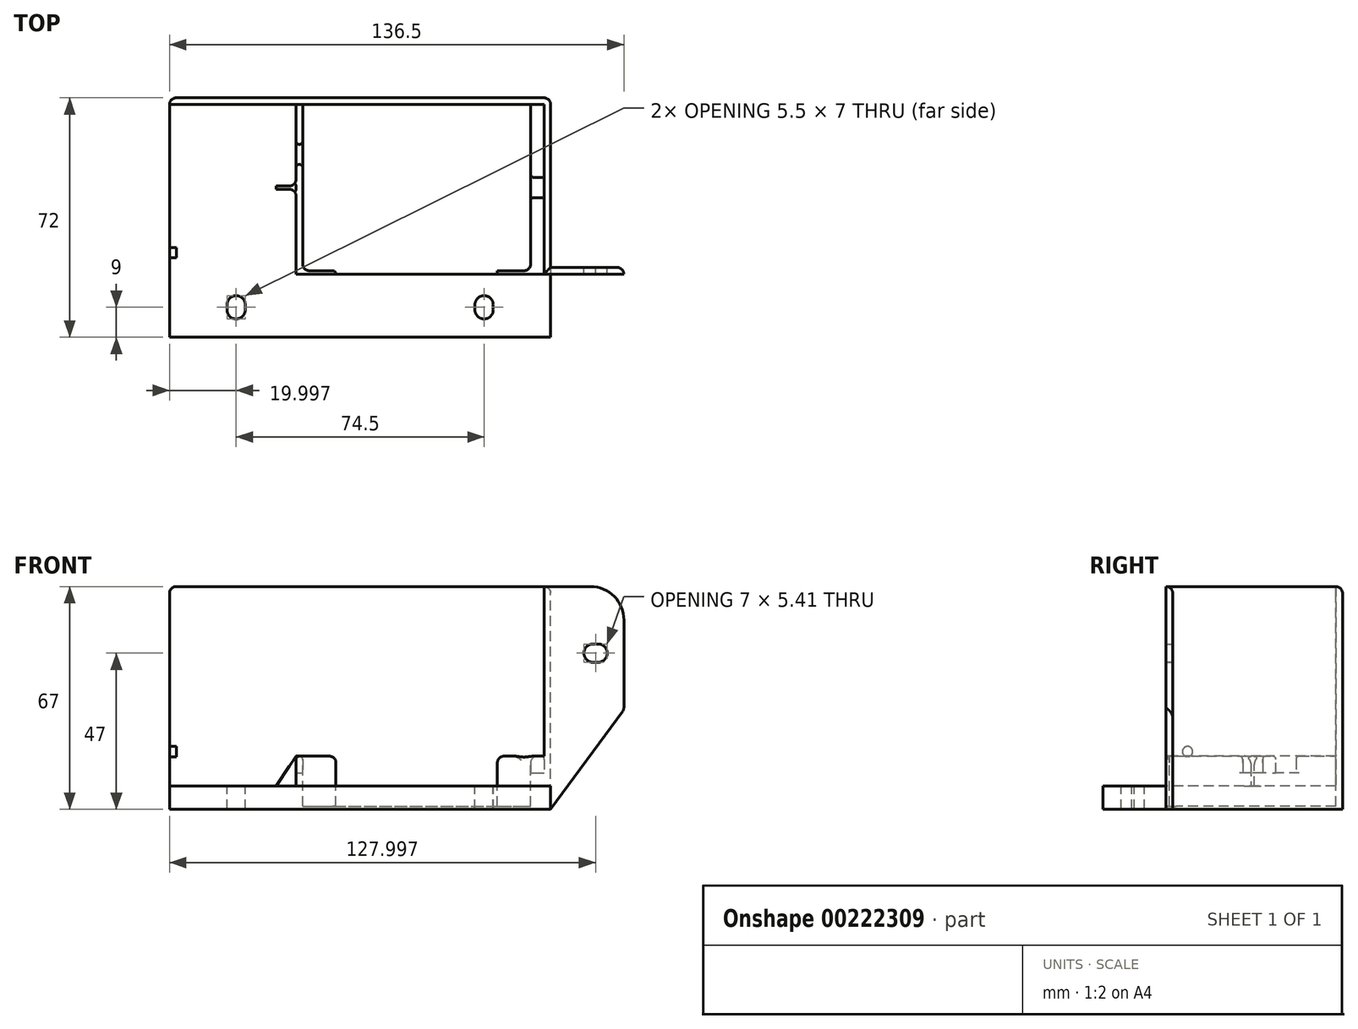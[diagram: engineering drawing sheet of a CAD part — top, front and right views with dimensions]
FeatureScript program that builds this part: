
annotation { "Feature Type Name" : "Feature", "Feature Type Description" : "" }
export const myFeature = defineFeature(function(context is Context, id is Id, definition is map)
    precondition{}
    {
        {
            var Q0;
            Q0=qCreatedBy(makeId("Top.planeOp"),FACE);
            var sketch = newSketch(context, id + "F0", { "sketchPlane" : qUnion([Q0])});
            skLineSegment(sketch, "E0.bottom", {"start": v(-55.25, 40.13) * mm, "end": v(59.25, 40.13) * mm});
            skLineSegment(sketch, "E0.top", {"start": v(-55.25, -31.87) * mm, "end": v(59.25, -31.87) * mm});
            skLineSegment(sketch, "E0.left", {"start": v(-55.25, 40.13) * mm, "end": v(-55.25, -31.87) * mm});
            skLineSegment(sketch, "E0.right", {"start": v(59.25, 40.13) * mm, "end": v(59.25, -31.87) * mm});
            skLineSegment(sketch, "E1", {"start": v(-55.25, -12.87) * mm, "end": v(59.25, -12.87) * mm, "construction": true});
            skLineSegment(sketch, "E2", {"start": v(-53.25, -12.87) * mm, "end": v(-53.25, 38.13) * mm});
            skLineSegment(sketch, "E3", {"start": v(-53.25, 38.13) * mm, "end": v(57.25, 38.13) * mm});
            skLineSegment(sketch, "E4", {"start": v(57.25, 38.13) * mm, "end": v(57.25, -12.87) * mm});
            skLineSegment(sketch, "E5", {"start": v(-55.25, -12.87) * mm, "end": v(-53.25, -12.87) * mm});
            skLineSegment(sketch, "E6", {"start": v(59.25, -12.87) * mm, "end": v(57.25, -12.87) * mm});
            skLineSegment(sketch, "E7", {"start": v(-55.25, -22.87) * mm, "end": v(59.25, -22.87) * mm, "construction": true});
            skCircle(sketch, "E8", {"center": v(-35.25, -22.87) * mm, "radius": 2.75 * mm});
            skCircle(sketch, "E9", {"center": v(39.25, -22.87) * mm, "radius": 2.75 * mm});
            skLineSegment(sketch, "E10", {"start": v(-15.25, 38.13) * mm, "end": v(-15.25, -11.87) * mm});
            skLineSegment(sketch, "E11", {"start": v(-15.25, -11.87) * mm, "end": v(-5.25, -11.87) * mm});
            skLineSegment(sketch, "E12", {"start": v(-17.25, 38.13) * mm, "end": v(-17.25, -12.87) * mm});
            skLineSegment(sketch, "E13", {"start": v(-17.25, -12.87) * mm, "end": v(57.25, -12.87) * mm});
            skLineSegment(sketch, "E14", {"start": v(53.25, 38.13) * mm, "end": v(53.25, -11.87) * mm});
            skLineSegment(sketch, "E15", {"start": v(53.25, 13.13) * mm, "end": v(57.25, 13.13) * mm, "construction": true});
            skLineSegment(sketch, "E16", {"start": v(53.25, 16.13) * mm, "end": v(57.25, 16.13) * mm});
            skLineSegment(sketch, "E17.MirrorCS", {"start": v(53.25, 10.13) * mm, "end": v(57.25, 10.13) * mm});
            skLineSegment(sketch, "E18", {"start": v(-17.25, 26.13) * mm, "end": v(-15.25, 26.13) * mm});
            skLineSegment(sketch, "E19", {"start": v(-17.25, 20.13) * mm, "end": v(-15.25, 20.13) * mm});
            skLineSegment(sketch, "E20", {"start": v(59.25, -12.87) * mm, "end": v(81.25, -12.87) * mm});
            skLineSegment(sketch, "E21", {"start": v(81.25, -12.87) * mm, "end": v(81.25, -10.87) * mm});
            skLineSegment(sketch, "E22", {"start": v(81.25, -10.87) * mm, "end": v(59.25, -10.87) * mm});
            skCircle(sketch, "E23", {"center": v(-35.25, -22.12) * mm, "radius": 2.75 * mm});
            skCircle(sketch, "E24", {"center": v(39.25, -22.12) * mm, "radius": 2.75 * mm});
            skCircle(sketch, "E25.MirrorC", {"center": v(-35.25, -23.62) * mm, "radius": 2.75 * mm});
            skCircle(sketch, "E26.MirrorC", {"center": v(39.25, -23.62) * mm, "radius": 2.75 * mm});
            skLineSegment(sketch, "E27", {"start": v(-5.25, -11.87) * mm, "end": v(-5.25, -12.87) * mm});
            skLineSegment(sketch, "E28", {"start": v(43.25, -11.87) * mm, "end": v(43.25, -12.87) * mm});
            skLineSegment(sketch, "E29.trimOffspring", {"start": v(43.25, -11.87) * mm, "end": v(57.25, -11.87) * mm});
            skPoint(sketch, "E30.oppositeSnap0", {"position": v(-17.25, 12.63) * mm});
            skLineSegment(sketch, "E30.bottom", {"start": v(-17.25, 13.63) * mm, "end": v(-27.25, 13.63) * mm});
            skLineSegment(sketch, "E30.top", {"start": v(-17.25, 12.63) * mm, "end": v(-27.25, 12.63) * mm});
            skLineSegment(sketch, "E30.left", {"start": v(-17.25, 13.63) * mm, "end": v(-17.25, 12.63) * mm});
            skLineSegment(sketch, "E30.right", {"start": v(-27.25, 13.63) * mm, "end": v(-27.25, 12.63) * mm});
            skSolve(sketch);
        }
        {
            var Q0;
            {var subQ9=sQuery(id+"F0.wireOp",EDGE,"E0.bottom");Q0=makeQuery(id+"F0.imprint","IMPRINT",FACE,{"disambiguationData":[TD([[makeQuery(id+"F0.imprint","IMPRINT",EDGE,{"derivedFrom":subQ9}),-1.0]])]});}
            var Q1;
            {var subQ28=sQuery(id+"F0.wireOp",EDGE,"E0.top");Q1=makeQuery(id+"F0.imprint","IMPRINT",FACE,{"disambiguationData":[TD([[makeQuery(id+"F0.imprint","IMPRINT",EDGE,{"derivedFrom":subQ28}),1.0]])]});}
            var Q2;
            {var subQ5=sQuery(id+"F0.wireOp",EDGE,"E18");Q2=makeQuery(id+"F0.imprint","IMPRINT",FACE,{"disambiguationData":[TD([[makeQuery(id+"F0.imprint","IMPRINT",EDGE,{"derivedFrom":subQ5}),1.0]])]});}
            var Q3;
            {var subQ0=sQuery(id+"F0.wireOp",EDGE,"E18");Q3=makeQuery(id+"F0.imprint","IMPRINT",FACE,{"disambiguationData":[TD([[makeQuery(id+"F0.imprint","IMPRINT",EDGE,{"derivedFrom":subQ0}),-1.0]])]});}
            var Q4;
            {var subQ2=sQuery(id+"F0.wireOp",EDGE,"E28");Q4=makeQuery(id+"F0.imprint","IMPRINT",FACE,{"disambiguationData":[TD([[makeQuery(id+"F0.imprint","IMPRINT",EDGE,{"derivedFrom":subQ2}),1.0]])]});}
            var Q5;
            {var subQ10=sQuery(id+"F0.wireOp",EDGE,"E11");Q5=makeQuery(id+"F0.imprint","IMPRINT",FACE,{"disambiguationData":[TD([[makeQuery(id+"F0.imprint","IMPRINT",EDGE,{"derivedFrom":subQ10}),1.0]])]});}
            var Q6;
            {var subQ5=sQuery(id+"F0.wireOp",EDGE,"E16");Q6=makeQuery(id+"F0.imprint","IMPRINT",FACE,{"disambiguationData":[TD([[makeQuery(id+"F0.imprint","IMPRINT",EDGE,{"derivedFrom":subQ5}),1.0]])]});}
            var Q7;
            {var subQ0=sQuery(id+"F0.wireOp",EDGE,"E16");Q7=makeQuery(id+"F0.imprint","IMPRINT",FACE,{"disambiguationData":[TD([[makeQuery(id+"F0.imprint","IMPRINT",EDGE,{"derivedFrom":subQ0}),-1.0]])]});}
            var Q8;
            {var subQ0=sQuery(id+"F0.wireOp",EDGE,"E17.MirrorCS");Q8=makeQuery(id+"F0.imprint","IMPRINT",FACE,{"disambiguationData":[TD([[makeQuery(id+"F0.imprint","IMPRINT",EDGE,{"derivedFrom":subQ0}),-1.0]])]});}
            var Q9;
            {var subQ4=sQuery(id+"F0.wireOp",EDGE,"E11");Q9=makeQuery(id+"F0.imprint","IMPRINT",FACE,{"disambiguationData":[TD([[makeQuery(id+"F0.imprint","IMPRINT",EDGE,{"derivedFrom":subQ4}),-1.0]])]});}
            var Q10;
            Q10=makeQuery(id+"F0.imprint","IMPRINT",FACE,{"disambiguationData":[TD([[makeQuery(id+"F0.imprint","IMPRINT",EDGE,{"derivedFrom":sQuery(id+"F0.wireOp",EDGE,"E30.bottom")}),1.0]])]});
            var Q11;
            {var subQ0=sQuery(id+"F0.wireOp",EDGE,"E20");Q11=makeQuery(id+"F0.imprint","IMPRINT",FACE,{"disambiguationData":[TD([[makeQuery(id+"F0.imprint","IMPRINT",EDGE,{"derivedFrom":subQ0}),1.0]])]});}
            extrude(context, id + "F1", {"entities" : qUnion([Q0, Q1, Q2, Q3, Q4, Q5, Q6, Q7, Q8, Q9, Q10, Q11]), "oppositeDirection" : true, "depth" : 7 * mm});
        }
        {
            var Q0;
            {var subQ1=sQuery(id+"F0.wireOp",EDGE,"E0.bottom");Q0=makeQuery(id+"F0.imprint","IMPRINT",FACE,{"disambiguationData":[TD([[makeQuery(id+"F0.imprint","IMPRINT",EDGE,{"derivedFrom":subQ1}),-1.0]])]});}
            extrude(context, id + "F2", {"entities" : qUnion([Q0]), "operationType" : NewBodyOperationType.ADD, "depth" : 60 * mm});
        }
        {
            var Q0;
            {var subQ10=sQuery(id+"F0.wireOp",EDGE,"E11");Q0=makeQuery(id+"F0.imprint","IMPRINT",FACE,{"disambiguationData":[TD([[makeQuery(id+"F0.imprint","IMPRINT",EDGE,{"derivedFrom":subQ10}),1.0]])]});}
            extrude(context, id + "F3", {"entities" : qUnion([Q0]), "operationType" : NewBodyOperationType.REMOVE, "oppositeDirection" : true, "depth" : 6 * mm});
        }
        {
            var Q0;
            Q0=makeQuery(id+"F2.opExtrude","CAP_FACE",FACE,{"disambiguationData":[OSD([sQuery(id+"F0.wireOp",EDGE,"E0.bottom"),sQuery(id+"F0.wireOp",EDGE,"E0.left"),sQuery(id+"F0.wireOp",EDGE,"E0.right"),sQuery(id+"F0.wireOp",EDGE,"E2"),sQuery(id+"F0.wireOp",EDGE,"E3"),sQuery(id+"F0.wireOp",EDGE,"E4"),sQuery(id+"F0.wireOp",EDGE,"E5"),sQuery(id+"F0.wireOp",EDGE,"E6")])],"isStart":false});
            var sketch = newSketch(context, id + "F4", { "sketchPlane" : qUnion([Q0])});
            skPoint(sketch, "E31.0", {"position": v(-55.25, 13.63) * mm});
            skLineSegment(sketch, "E32.0", {"start": v(-55.25, 40.13) * mm, "end": v(-55.25, -12.87) * mm, "construction": true});
            skLineSegment(sketch, "E33.0", {"start": v(-53.25, -12.87) * mm, "end": v(-53.25, 38.13) * mm, "construction": true});
            skLineSegment(sketch, "E34.0", {"start": v(-55.25, -12.87) * mm, "end": v(-53.25, -12.87) * mm, "construction": true});
            skLineSegment(sketch, "E35", {"start": v(-53.25, 12.63) * mm, "end": v(-55.25, 12.63) * mm, "construction": true});
            skLineSegment(sketch, "E36", {"start": v(-55.25, 6.63) * mm, "end": v(-53.25, 6.63) * mm});
            skLineSegment(sketch, "E37.MirrorCS", {"start": v(-55.25, 18.63) * mm, "end": v(-53.25, 18.63) * mm});
            skLineSegment(sketch, "E38", {"start": v(-55.25, 18.63) * mm, "end": v(-55.25, 6.63) * mm});
            skLineSegment(sketch, "E39", {"start": v(-53.25, 18.63) * mm, "end": v(-53.25, 6.63) * mm});
            skSolve(sketch);
        }
        {
            var Q0;
            Q0=makeQuery(id+"F4.imprint","IMPRINT",FACE,{"disambiguationData":[TD([[makeQuery(id+"F4.imprint","IMPRINT",EDGE,{"derivedFrom":sQuery(id+"F4.wireOp",EDGE,"E36")}),1.0]])]});
            extrude(context, id + "F5", {"entities" : qUnion([Q0]), "operationType" : NewBodyOperationType.ADD, "depth" : 6 * mm});
        }
        {
            var Q0;
            Q0=makeQuery(id+"F5.opExtrude","CAP_EDGE",EDGE,{"disambiguationData":[OSD([sQuery(id+"F4.wireOp",EDGE,"E36")])],"isStart":true});
            var Q1;
            Q1=makeQuery(id+"F5.opExtrude","CAP_EDGE",EDGE,{"disambiguationData":[OSD([sQuery(id+"F4.wireOp",EDGE,"E36")])],"isStart":false});
            var Q2;
            Q2=makeQuery(id+"F5.opExtrude","CAP_EDGE",EDGE,{"disambiguationData":[OSD([sQuery(id+"F4.wireOp",EDGE,"E37.MirrorCS")])],"isStart":false});
            var Q3;
            Q3=makeQuery(id+"F5.opExtrude","CAP_EDGE",EDGE,{"disambiguationData":[OSD([sQuery(id+"F4.wireOp",EDGE,"E37.MirrorCS")])],"isStart":true});
            fillet(context, id + "F6", {"entities" : qUnion([Q0, Q1, Q2, Q3]), "radius" : 2.5 * mm, "tangentPropagation" : true, "allowEdgeOverflow" : false});
        }
        {
            var Q0;
            {var subQ0=sQuery(id+"F0.wireOp",EDGE,"E20");Q0=makeQuery(id+"F0.imprint","IMPRINT",FACE,{"disambiguationData":[TD([[makeQuery(id+"F0.imprint","IMPRINT",EDGE,{"derivedFrom":subQ0}),1.0]])]});}
            extrude(context, id + "F7", {"entities" : qUnion([Q0]), "operationType" : NewBodyOperationType.ADD, "depth" : 60 * mm});
        }
        {
            var Q0;
            {var subQ0=sQuery(id+"F0.wireOp",EDGE,"E18");Q0=makeQuery(id+"F0.imprint","IMPRINT",FACE,{"disambiguationData":[TD([[makeQuery(id+"F0.imprint","IMPRINT",EDGE,{"derivedFrom":subQ0}),-1.0]])]});}
            var Q1;
            {var subQ0=sQuery(id+"F0.wireOp",EDGE,"E16");Q1=makeQuery(id+"F0.imprint","IMPRINT",FACE,{"disambiguationData":[TD([[makeQuery(id+"F0.imprint","IMPRINT",EDGE,{"derivedFrom":subQ0}),-1.0]])]});}
            extrude(context, id + "F8", {"entities" : qUnion([Q0, Q1]), "operationType" : NewBodyOperationType.ADD, "depth" : 4 * mm});
        }
        {
            var Q0;
            {var subQ5=sQuery(id+"F0.wireOp",EDGE,"E18");Q0=makeQuery(id+"F0.imprint","IMPRINT",FACE,{"disambiguationData":[TD([[makeQuery(id+"F0.imprint","IMPRINT",EDGE,{"derivedFrom":subQ5}),1.0]])]});}
            var Q1;
            {var subQ7=sQuery(id+"F0.wireOp",EDGE,"E13");Q1=makeQuery(id+"F0.imprint","IMPRINT",FACE,{"disambiguationData":[TD([[makeQuery(id+"F0.imprint","IMPRINT",EDGE,{"derivedFrom":subQ7}),1.0]])]});}
            var Q2;
            {var subQ5=sQuery(id+"F0.wireOp",EDGE,"E16");Q2=makeQuery(id+"F0.imprint","IMPRINT",FACE,{"disambiguationData":[TD([[makeQuery(id+"F0.imprint","IMPRINT",EDGE,{"derivedFrom":subQ5}),1.0]])]});}
            var Q3;
            {var subQ3=sQuery(id+"F0.wireOp",EDGE,"E17.MirrorCS");Q3=makeQuery(id+"F0.imprint","IMPRINT",FACE,{"disambiguationData":[TD([[makeQuery(id+"F0.imprint","IMPRINT",EDGE,{"derivedFrom":subQ3}),-1.0]])]});}
            var Q4;
            {var subQ4=sQuery(id+"F0.wireOp",EDGE,"E11");Q4=makeQuery(id+"F0.imprint","IMPRINT",FACE,{"disambiguationData":[TD([[makeQuery(id+"F0.imprint","IMPRINT",EDGE,{"derivedFrom":subQ4}),-1.0]])]});}
            var Q5;
            Q5=makeQuery(id+"F0.imprint","IMPRINT",FACE,{"disambiguationData":[TD([[makeQuery(id+"F0.imprint","IMPRINT",EDGE,{"derivedFrom":sQuery(id+"F0.wireOp",EDGE,"E30.bottom")}),1.0]])]});
            extrude(context, id + "F9", {"entities" : qUnion([Q0, Q1, Q2, Q3, Q4, Q5]), "operationType" : NewBodyOperationType.ADD, "depth" : 9 * mm});
        }
        {
            var Q0;
            Q0=makeQuery(id+"F2.opExtrude","SWEPT_FACE",FACE,{"disambiguationData":[OSD([sQuery(id+"F0.wireOp",EDGE,"E2")])]});
            var sketch = newSketch(context, id + "F10", { "sketchPlane" : qUnion([Q0])});
            skLineSegment(sketch, "E40.0.0", {"start": v(-12.87, 0) * mm, "end": v(38.13, 0) * mm, "construction": true});
            skLineSegment(sketch, "E40.0.1", {"start": v(38.13, 0) * mm, "end": v(38.13, 60) * mm, "construction": true});
            skLineSegment(sketch, "E40.0.2", {"start": v(38.13, 60) * mm, "end": v(-12.87, 60) * mm, "construction": true});
            skLineSegment(sketch, "E40.0.3", {"start": v(-12.87, 60) * mm, "end": v(-12.87, 0) * mm, "construction": true});
            skLineSegment(sketch, "E41.0.0", {"start": v(38.13, -6.5) * mm, "end": v(-12.87, -6.5) * mm, "construction": true});
            skLineSegment(sketch, "E41.0.1", {"start": v(-12.87, -6.5) * mm, "end": v(-12.87, 10.5) * mm, "construction": true});
            skLineSegment(sketch, "E41.0.2", {"start": v(-12.87, 10.5) * mm, "end": v(20.13, 10.5) * mm, "construction": true});
            skLineSegment(sketch, "E41.0.6", {"start": v(25.88, 17) * mm, "end": v(37.88, 17) * mm, "construction": true});
            skLineSegment(sketch, "E42.0", {"start": v(38.13, 0) * mm, "end": v(-12.87, 0) * mm, "construction": true});
            skLineSegment(sketch, "E42.3", {"start": v(38.13, 0) * mm, "end": v(-12.87, 0) * mm, "construction": true});
            skLineSegment(sketch, "E42.8", {"start": v(38.13, 0) * mm, "end": v(-11.87, 0) * mm, "construction": true});
            skLineSegment(sketch, "E42.9", {"start": v(38.13, 0) * mm, "end": v(-12.87, 0) * mm, "construction": true});
            skLineSegment(sketch, "E42.14", {"start": v(38.13, 0) * mm, "end": v(-12.87, 0) * mm, "construction": true});
            skLineSegment(sketch, "E42.15", {"start": v(38.13, 0) * mm, "end": v(-11.87, 0) * mm, "construction": true});
            skLineSegment(sketch, "E43.bottom", {"start": v(3.07, 20.3) * mm, "end": v(23.67, 20.3) * mm});
            skLineSegment(sketch, "E43.top", {"start": v(3.07, 0.5) * mm, "end": v(23.67, 0.5) * mm});
            skLineSegment(sketch, "E43.left", {"start": v(-0.43, 16.8) * mm, "end": v(-0.43, 4) * mm});
            skLineSegment(sketch, "E43.right", {"start": v(27.17, 16.8) * mm, "end": v(27.17, 4) * mm});
            skPoint(sketch, "E44.visualSharp", {"position": v(-0.43, 20.3) * mm});
            skArc(sketch, "E44.filletArc", {"start": v(3.07, 20.3) * mm, "mid": v(0.6, 19.27) * mm, "end": v(-0.43, 16.8) * mm});
            skPoint(sketch, "E45.visualSharp", {"position": v(27.17, 20.3) * mm});
            skArc(sketch, "E45.filletArc", {"start": v(27.17, 16.8) * mm, "mid": v(26.15, 19.27) * mm, "end": v(23.67, 20.3) * mm});
            skPoint(sketch, "E46.visualSharp", {"position": v(27.17, 0.5) * mm});
            skArc(sketch, "E46.filletArc", {"start": v(23.67, 0.5) * mm, "mid": v(26.15, 1.53) * mm, "end": v(27.17, 4) * mm});
            skPoint(sketch, "E47.visualSharp", {"position": v(-0.43, 0.5) * mm});
            skArc(sketch, "E47.filletArc", {"start": v(-0.43, 4) * mm, "mid": v(0.6, 1.53) * mm, "end": v(3.07, 0.5) * mm});
            skLineSegment(sketch, "E48", {"start": v(-0.43, 10.4) * mm, "end": v(53.34, 10.4) * mm, "construction": true});
            skPoint(sketch, "E48.endSnap0", {"position": v(27.17, 10.4) * mm});
            skLineSegment(sketch, "E49", {"start": v(13.37, 20.3) * mm, "end": v(13.37, 0.5) * mm, "construction": true});
            skCircle(sketch, "E50", {"center": v(33.17, 10.4) * mm, "radius": 1.55 * mm});
            skPoint(sketch, "E50.centerSnap0", {"position": v(33.17, 10.75) * mm});
            skCircle(sketch, "E51.MirrorC", {"center": v(-6.43, 10.4) * mm, "radius": 1.55 * mm});
            skCircle(sketch, "E52", {"center": v(12.63, 60.75) * mm, "radius": 1.6 * mm});
            skLineSegment(sketch, "E53.bottom", {"start": v(33.87, 38.3) * mm, "end": v(14.87, 38.3) * mm});
            skLineSegment(sketch, "E53.top", {"start": v(33.87, 25.3) * mm, "end": v(14.87, 25.3) * mm});
            skLineSegment(sketch, "E53.left", {"start": v(33.87, 38.3) * mm, "end": v(33.87, 25.3) * mm});
            skLineSegment(sketch, "E53.right", {"start": v(14.87, 38.3) * mm, "end": v(14.87, 25.3) * mm});
            skLineSegment(sketch, "E54", {"start": v(24.37, 38.3) * mm, "end": v(24.37, 25.3) * mm, "construction": true});
            skSolve(sketch);
        }
        {
            var Q0;
            Q0=makeQuery(id+"F10.imprint","IMPRINT",FACE,{"disambiguationData":[TD([[makeQuery(id+"F10.imprint","IMPRINT",EDGE,{"derivedFrom":sQuery(id+"F10.wireOp",EDGE,"E43.bottom")}),-1.0]])]});
            var Q1;
            Q1=makeQuery(id+"F10.imprint","IMPRINT",FACE,{"disambiguationData":[TD([[makeQuery(id+"F10.imprint","IMPRINT",EDGE,{"derivedFrom":sQuery(id+"F10.wireOp",EDGE,"E50")}),1.0]])]});
            var Q2;
            Q2=makeQuery(id+"F10.imprint","IMPRINT",FACE,{"disambiguationData":[TD([[makeQuery(id+"F10.imprint","IMPRINT",EDGE,{"derivedFrom":sQuery(id+"F10.wireOp",EDGE,"E51.MirrorC")}),-1.0]])]});
            var Q3;
            Q3=makeQuery(id+"F10.imprint","IMPRINT",FACE,{"disambiguationData":[TD([[makeQuery(id+"F10.imprint","IMPRINT",EDGE,{"derivedFrom":sQuery(id+"F10.wireOp",EDGE,"E52")}),1.0]])]});
            var Q4;
            Q4=makeQuery(id+"F10.imprint","IMPRINT",FACE,{"disambiguationData":[TD([[makeQuery(id+"F10.imprint","IMPRINT",EDGE,{"derivedFrom":sQuery(id+"F10.wireOp",EDGE,"E53.bottom")}),1.0]])]});
            extrude(context, id + "F11", {"entities" : qUnion([Q0, Q1, Q2, Q3, Q4]), "operationType" : NewBodyOperationType.REMOVE, "endBound" : BoundingType.THROUGH_ALL, "oppositeDirection" : true, "depth" : 25 * mm});
        }
        {
            var Q0;
            Q0=makeQuery(id+"F7.opExtrude","CAP_EDGE",EDGE,{"disambiguationData":[OSD([sQuery(id+"F0.wireOp",EDGE,"E21")])],"isStart":false});
            var Q1;
            Q1=makeQuery(id+"F2.opExtrude","CAP_EDGE",EDGE,{"disambiguationData":[OSD([sQuery(id+"F0.wireOp",EDGE,"E5")])],"isStart":false});
            fillet(context, id + "F12", {"entities" : qUnion([Q0, Q1]), "radius" : 10 * mm, "tangentPropagation" : true, "allowEdgeOverflow" : false});
        }
        {
            var Q0;
            Q0=makeQuery(id+"F9.opExtrude","CAP_EDGE",EDGE,{"disambiguationData":[OSD([sQuery(id+"F0.wireOp",EDGE,"E30.right")])],"isStart":false});
            chamfer(context, id + "F13", {"entities" : qUnion([Q0]), "chamferType" : ChamferType.TWO_OFFSETS, "width1" : 10 * mm, "oppositeDirection" : false, "width2" : 15 * mm, "tangentPropagation" : true});
        }
        {
            var Q0;
            Q0=makeQuery(id+"F1.opExtrude","CAP_EDGE",EDGE,{"disambiguationData":[OSD([sQuery(id+"F0.wireOp",EDGE,"E21")])],"isStart":false});
            chamfer(context, id + "F14", {"entities" : qUnion([Q0]), "chamferType" : ChamferType.TWO_OFFSETS, "width1" : 30 * mm, "oppositeDirection" : false, "width2" : 22 * mm, "tangentPropagation" : true});
        }
        {
            var Q0;
            {var subQ0=sQuery(id+"F0.wireOp",EDGE,"E0.right");var subQ1=sQuery(id+"F0.wireOp",EDGE,"E0.bottom");Q0=makeQuery(id+"F2.boolean.opBoolean","MERGE",EDGE,{"derivedFrom":[makeQuery(id+"F1.opExtrude","SWEPT_EDGE",EDGE,{"disambiguationData":[OSD([subQ1,subQ0])]}),makeQuery(id+"F2.opExtrude","SWEPT_EDGE",EDGE,{"disambiguationData":[OSD([subQ1,subQ0])]})]});}
            var Q1;
            Q1=makeQuery(id+"F2.opExtrude","CAP_EDGE",EDGE,{"disambiguationData":[OSD([sQuery(id+"F0.wireOp",EDGE,"E0.right")])],"isStart":false});
            var Q2;
            Q2=makeQuery(id+"F7.opExtrude","CAP_EDGE",EDGE,{"disambiguationData":[OSD([sQuery(id+"F0.wireOp",EDGE,"E22")])],"isStart":false});
            var Q3;
            Q3=makeQuery(id+"F2.opExtrude","CAP_EDGE",EDGE,{"disambiguationData":[OSD([sQuery(id+"F0.wireOp",EDGE,"E0.bottom")])],"isStart":false});
            var Q4;
            {var subQ0=sQuery(id+"F0.wireOp",EDGE,"E22");var subQ1=sQuery(id+"F0.wireOp",EDGE,"E0.right");Q4=makeQuery(id+"F7.boolean.opBoolean","MERGE",EDGE,{"derivedFrom":[makeQuery(id+"F1.opExtrude","SWEPT_EDGE",EDGE,{"disambiguationData":[OSD([subQ1,subQ0])]}),makeQuery(id+"F7.opExtrude","SWEPT_EDGE",EDGE,{"disambiguationData":[OSD([subQ1,subQ0])]})]});}
            var Q5;
            {var subQ0=sQuery(id+"F0.wireOp",EDGE,"E22");var subQ1=sQuery(id+"F0.wireOp",EDGE,"E21");Q5=makeQuery(id+"F7.boolean.opBoolean","MERGE",EDGE,{"derivedFrom":[makeQuery(id+"F1.opExtrude","SWEPT_EDGE",EDGE,{"disambiguationData":[OSD([subQ1,subQ0])]}),makeQuery(id+"F7.opExtrude","SWEPT_EDGE",EDGE,{"disambiguationData":[OSD([subQ1,subQ0])]})]});}
            var Q6;
            {var subQ0=sQuery(id+"F0.wireOp",EDGE,"E0.left");var subQ1=sQuery(id+"F0.wireOp",EDGE,"E0.bottom");Q6=makeQuery(id+"F2.boolean.opBoolean","MERGE",EDGE,{"derivedFrom":[makeQuery(id+"F1.opExtrude","SWEPT_EDGE",EDGE,{"disambiguationData":[OSD([subQ1,subQ0])]}),makeQuery(id+"F2.opExtrude","SWEPT_EDGE",EDGE,{"disambiguationData":[OSD([subQ1,subQ0])]})]});}
            var Q7;
            {var subQ0=sQuery(id+"F0.wireOp",EDGE,"E0.left");var subQ1=sQuery(id+"F0.wireOp",EDGE,"E0.bottom");Q7=makeQuery(id+"F5.boolean.opBoolean","SPLIT",EDGE,{"disambiguationData":[TD([makeQuery(id+"F1.opExtrude","SWEPT_FACE",FACE,{"disambiguationData":[OSD([subQ1])]})])],"derivedFrom":makeQuery(id+"F2.opExtrude","CAP_EDGE",EDGE,{"disambiguationData":[OSD([subQ0])],"isStart":false})});}
            var Q8;
            Q8=makeQuery(id+"F2.opExtrude","SWEPT_EDGE",EDGE,{"disambiguationData":[OSD([sQuery(id+"F0.wireOp",EDGE,"E0.left"),sQuery(id+"F0.wireOp",EDGE,"E5")])]});
            var Q9;
            {var subQ0=sQuery(id+"F0.wireOp",EDGE,"E14");Q9=makeQuery(id+"F9.opExtrude","CAP_EDGE",EDGE,{"disambiguationData":[OSD([subQ0]),TDD([makeQuery(id+"F0.imprint","IMPRINT",EDGE,{"disambiguationData":[TD([[makeQuery(id+"F0.imprint","INTERSECT",VERTEX,{"derivedFrom":[sQuery(id+"F0.wireOp",EDGE,"E3"),subQ0]}),-1.0]])],"derivedFrom":subQ0})])],"isStart":false});}
            var Q10;
            {var subQ0=sQuery(id+"F0.wireOp",EDGE,"E14");Q10=makeQuery(id+"F9.opExtrude","CAP_EDGE",EDGE,{"disambiguationData":[OSD([subQ0]),TDD([makeQuery(id+"F0.imprint","IMPRINT",EDGE,{"disambiguationData":[TD([[makeQuery(id+"F0.imprint","INTERSECT",VERTEX,{"derivedFrom":[sQuery(id+"F0.wireOp",EDGE,"E11"),subQ0]}),1.0]])],"derivedFrom":subQ0})])],"isStart":false});}
            var Q11;
            Q11=makeQuery(id+"F9.opExtrude","CAP_EDGE",EDGE,{"disambiguationData":[OSD([sQuery(id+"F0.wireOp",EDGE,"E28")])],"isStart":false});
            var Q12;
            Q12=makeQuery(id+"F9.opExtrude","CAP_EDGE",EDGE,{"disambiguationData":[OSD([sQuery(id+"F0.wireOp",EDGE,"E28")])],"isStart":true});
            var Q13;
            Q13=makeQuery(id+"F9.opExtrude","CAP_EDGE",EDGE,{"disambiguationData":[OSD([sQuery(id+"F0.wireOp",EDGE,"E27")])],"isStart":false});
            var Q14;
            Q14=makeQuery(id+"F9.opExtrude","CAP_EDGE",EDGE,{"disambiguationData":[OSD([sQuery(id+"F0.wireOp",EDGE,"E27")])],"isStart":true});
            var Q15;
            Q15=makeQuery(id+"F9.opExtrude","SWEPT_EDGE",EDGE,{"disambiguationData":[OSD([sQuery(id+"F0.wireOp",EDGE,"E10"),sQuery(id+"F0.wireOp",EDGE,"E11")])]});
            var Q16;
            Q16=makeQuery(id+"F9.opExtrude","SWEPT_EDGE",EDGE,{"disambiguationData":[OSD([sQuery(id+"F0.wireOp",EDGE,"E14"),sQuery(id+"F0.wireOp",EDGE,"E29.trimOffspring")])]});
            var Q17;
            Q17=makeQuery(id+"F9.opExtrude","SWEPT_EDGE",EDGE,{"disambiguationData":[OSD([sQuery(id+"F0.wireOp",EDGE,"E3"),sQuery(id+"F0.wireOp",EDGE,"E10")])]});
            var Q18;
            Q18=makeQuery(id+"F9.opExtrude","SWEPT_EDGE",EDGE,{"disambiguationData":[OSD([sQuery(id+"F0.wireOp",EDGE,"E3"),sQuery(id+"F0.wireOp",EDGE,"E12")])]});
            var Q19;
            Q19=makeQuery(id+"F9.opExtrude","SWEPT_EDGE",EDGE,{"disambiguationData":[OSD([sQuery(id+"F0.wireOp",EDGE,"E3"),sQuery(id+"F0.wireOp",EDGE,"E14")])]});
            var Q20;
            {var subQ0=sQuery(id+"F0.wireOp",EDGE,"E3");Q20=makeQuery(id+"F9.opExtrude","CAP_EDGE",EDGE,{"disambiguationData":[OSD([subQ0]),TDD([makeQuery(id+"F0.imprint","IMPRINT",EDGE,{"disambiguationData":[TD([[makeQuery(id+"F0.imprint","INTERSECT",VERTEX,{"derivedFrom":[subQ0,sQuery(id+"F0.wireOp",EDGE,"E10")]}),1.0]])],"derivedFrom":subQ0})])],"isStart":false});}
            var Q21;
            {var subQ0=sQuery(id+"F0.wireOp",EDGE,"E12");Q21=makeQuery(id+"F9.opExtrude","CAP_EDGE",EDGE,{"disambiguationData":[OSD([subQ0]),TDD([makeQuery(id+"F0.imprint","IMPRINT",EDGE,{"disambiguationData":[TD([[makeQuery(id+"F0.imprint","INTERSECT",VERTEX,{"derivedFrom":[subQ0,sQuery(id+"F0.wireOp",EDGE,"E13")]}),1.0]])],"derivedFrom":subQ0})])],"isStart":true});}
            var Q22;
            {var subQ0=sQuery(id+"F0.wireOp",EDGE,"E12");Q22=makeQuery(id+"F9.boolean.opBoolean","MERGE",EDGE,{"derivedFrom":[makeQuery(id+"F8.opExtrude","CAP_EDGE",EDGE,{"disambiguationData":[OSD([subQ0])],"isStart":true}),makeQuery(id+"F9.opExtrude","CAP_EDGE",EDGE,{"disambiguationData":[OSD([subQ0]),TDD([makeQuery(id+"F0.imprint","IMPRINT",EDGE,{"disambiguationData":[TD([[makeQuery(id+"F0.imprint","INTERSECT",VERTEX,{"derivedFrom":[sQuery(id+"F0.wireOp",EDGE,"E3"),subQ0]}),-1.0]])],"derivedFrom":subQ0})])],"isStart":true}),makeQuery(id+"F9.opExtrude","CAP_EDGE",EDGE,{"disambiguationData":[OSD([subQ0]),TDD([makeQuery(id+"F0.imprint","IMPRINT",EDGE,{"disambiguationData":[TD([[makeQuery(id+"F0.imprint","INTERSECT",VERTEX,{"derivedFrom":[subQ0,sQuery(id+"F0.wireOp",EDGE,"E19")]}),-1.0]])],"derivedFrom":subQ0})])],"isStart":true})]});}
            var Q23;
            {var subQ0=sQuery(id+"F0.wireOp",EDGE,"E10");Q23=makeQuery(id+"F9.boolean.opBoolean","MERGE",EDGE,{"derivedFrom":[makeQuery(id+"F8.opExtrude","CAP_EDGE",EDGE,{"disambiguationData":[OSD([subQ0])],"isStart":true}),makeQuery(id+"F9.opExtrude","CAP_EDGE",EDGE,{"disambiguationData":[OSD([subQ0]),TDD([makeQuery(id+"F0.imprint","IMPRINT",EDGE,{"disambiguationData":[TD([[makeQuery(id+"F0.imprint","INTERSECT",VERTEX,{"derivedFrom":[sQuery(id+"F0.wireOp",EDGE,"E3"),subQ0]}),-1.0]])],"derivedFrom":subQ0})])],"isStart":true}),makeQuery(id+"F9.opExtrude","CAP_EDGE",EDGE,{"disambiguationData":[OSD([subQ0]),TDD([makeQuery(id+"F0.imprint","IMPRINT",EDGE,{"disambiguationData":[TD([[makeQuery(id+"F0.imprint","INTERSECT",VERTEX,{"derivedFrom":[subQ0,sQuery(id+"F0.wireOp",EDGE,"E11")]}),1.0]])],"derivedFrom":subQ0})])],"isStart":true})]});}
            var Q24;
            Q24=makeQuery(id+"F9.opExtrude","CAP_EDGE",EDGE,{"disambiguationData":[OSD([sQuery(id+"F0.wireOp",EDGE,"E11")])],"isStart":true});
            var Q25;
            Q25=makeQuery(id+"F9.opExtrude","CAP_EDGE",EDGE,{"disambiguationData":[OSD([sQuery(id+"F0.wireOp",EDGE,"E29.trimOffspring")])],"isStart":true});
            var Q26;
            {var subQ0=sQuery(id+"F0.wireOp",EDGE,"E3");Q26=makeQuery(id+"F9.boolean.opBoolean","SPLIT",EDGE,{"disambiguationData":[TD([makeQuery(id+"F2.opExtrude","SWEPT_FACE",FACE,{"disambiguationData":[OSD([sQuery(id+"F0.wireOp",EDGE,"E2")])]})])],"derivedFrom":makeQuery(id+"F2.opExtrude","CAP_EDGE",EDGE,{"disambiguationData":[OSD([subQ0])],"isStart":true})});}
            var Q27;
            {var subQ1=sQuery(id+"F0.wireOp",EDGE,"E3");var subQ2=sQuery(id+"F0.wireOp",EDGE,"E10");Q27=makeQuery(id+"F9.boolean.opBoolean","SPLIT",EDGE,{"disambiguationData":[TD([makeQuery(id+"F8.opExtrude","SWEPT_FACE",FACE,{"disambiguationData":[OSD([subQ2])]})])],"derivedFrom":makeQuery(id+"F2.opExtrude","CAP_EDGE",EDGE,{"disambiguationData":[OSD([subQ1])],"isStart":true})});}
            var Q28;
            Q28=makeQuery(id+"F9.opExtrude","CAP_EDGE",EDGE,{"disambiguationData":[OSD([sQuery(id+"F0.wireOp",EDGE,"E30.top")])],"isStart":true});
            var Q29;
            Q29=makeQuery(id+"F9.opExtrude","CAP_EDGE",EDGE,{"disambiguationData":[OSD([sQuery(id+"F0.wireOp",EDGE,"E30.bottom")])],"isStart":true});
            var Q30;
            Q30=makeQuery(id+"F9.opExtrude","SWEPT_EDGE",EDGE,{"disambiguationData":[OSD([sQuery(id+"F0.wireOp",EDGE,"E12"),sQuery(id+"F0.wireOp",EDGE,"E30.top"),sQuery(id+"F0.wireOp",EDGE,"E30.left")])]});
            var Q31;
            Q31=makeQuery(id+"F9.opExtrude","SWEPT_EDGE",EDGE,{"disambiguationData":[OSD([sQuery(id+"F0.wireOp",EDGE,"E12"),sQuery(id+"F0.wireOp",EDGE,"E30.bottom"),sQuery(id+"F0.wireOp",EDGE,"E30.left")])]});
            var Q32;
            {var subQ0=sQuery(id+"F0.wireOp",EDGE,"E21");Q32=makeQuery(id+"F14.opChamfer","BLEND_EDGE",EDGE,{"blendedFrom":[makeQuery(id+"F1.opExtrude","CAP_EDGE",EDGE,{"disambiguationData":[OSD([subQ0])],"isStart":false}),makeQuery(id+"F7.boolean.opBoolean","MERGE",FACE,{"derivedFrom":[makeQuery(id+"F1.opExtrude","SWEPT_FACE",FACE,{"disambiguationData":[OSD([subQ0])]}),makeQuery(id+"F7.opExtrude","SWEPT_FACE",FACE,{"disambiguationData":[OSD([subQ0])]})]})],"blendedInto":[makeQuery(id+"F7.boolean.opBoolean","MERGE",FACE,{"derivedFrom":[makeQuery(id+"F1.opExtrude","SWEPT_FACE",FACE,{"disambiguationData":[OSD([subQ0])]}),makeQuery(id+"F7.opExtrude","SWEPT_FACE",FACE,{"disambiguationData":[OSD([subQ0])]})]})]});}
            fillet(context, id + "F15", {"entities" : qUnion([Q0, Q1, Q2, Q3, Q4, Q5, Q6, Q7, Q8, Q9, Q10, Q11, Q12, Q13, Q14, Q15, Q16, Q17, Q18, Q19, Q20, Q21, Q22, Q23, Q24, Q25, Q26, Q27, Q28, Q29, Q30, Q31, Q32]), "radius" : 2 * mm, "tangentPropagation" : true, "allowEdgeOverflow" : false});
        }
        {
            var Q0;
            {var subQ0=sQuery(id+"F0.wireOp",EDGE,"E12");Q0=makeQuery(id+"F9.opExtrude","CAP_EDGE",EDGE,{"disambiguationData":[OSD([subQ0]),TDD([makeQuery(id+"F0.imprint","IMPRINT",EDGE,{"disambiguationData":[TD([[makeQuery(id+"F0.imprint","INTERSECT",VERTEX,{"derivedFrom":[subQ0,sQuery(id+"F0.wireOp",EDGE,"E13")]}),1.0]])],"derivedFrom":subQ0})])],"isStart":false});}
            var Q1;
            {var subQ0=sQuery(id+"F0.wireOp",EDGE,"E10");Q1=makeQuery(id+"F9.opExtrude","CAP_EDGE",EDGE,{"disambiguationData":[OSD([subQ0]),TDD([makeQuery(id+"F0.imprint","IMPRINT",EDGE,{"disambiguationData":[TD([[makeQuery(id+"F0.imprint","INTERSECT",VERTEX,{"derivedFrom":[sQuery(id+"F0.wireOp",EDGE,"E3"),subQ0]}),-1.0]])],"derivedFrom":subQ0})])],"isStart":false});}
            var Q2;
            {var subQ0=sQuery(id+"F0.wireOp",EDGE,"E12");Q2=makeQuery(id+"F9.opExtrude","CAP_EDGE",EDGE,{"disambiguationData":[OSD([subQ0]),TDD([makeQuery(id+"F0.imprint","IMPRINT",EDGE,{"disambiguationData":[TD([[makeQuery(id+"F0.imprint","INTERSECT",VERTEX,{"derivedFrom":[sQuery(id+"F0.wireOp",EDGE,"E3"),subQ0]}),-1.0]])],"derivedFrom":subQ0})])],"isStart":false});}
            var Q3;
            Q3=makeQuery(id+"F9.opExtrude","CAP_EDGE",EDGE,{"disambiguationData":[OSD([sQuery(id+"F0.wireOp",EDGE,"E19")])],"isStart":false});
            var Q4;
            Q4=makeQuery(id+"F9.opExtrude","CAP_EDGE",EDGE,{"disambiguationData":[OSD([sQuery(id+"F0.wireOp",EDGE,"E18")])],"isStart":false});
            var Q5;
            {var subQ0=sQuery(id+"F0.wireOp",EDGE,"E10");Q5=makeQuery(id+"F9.opExtrude","CAP_EDGE",EDGE,{"disambiguationData":[OSD([subQ0]),TDD([makeQuery(id+"F0.imprint","IMPRINT",EDGE,{"disambiguationData":[TD([[makeQuery(id+"F0.imprint","INTERSECT",VERTEX,{"derivedFrom":[subQ0,sQuery(id+"F0.wireOp",EDGE,"E11")]}),1.0]])],"derivedFrom":subQ0})])],"isStart":false});}
            var Q6;
            Q6=makeQuery(id+"F8.opExtrude","CAP_EDGE",EDGE,{"disambiguationData":[OSD([sQuery(id+"F0.wireOp",EDGE,"E16")])],"isStart":false});
            var Q7;
            Q7=makeQuery(id+"F8.opExtrude","CAP_EDGE",EDGE,{"disambiguationData":[OSD([sQuery(id+"F0.wireOp",EDGE,"E17.MirrorCS")])],"isStart":false});
            var Q8;
            Q8=makeQuery(id+"F8.opExtrude","CAP_EDGE",EDGE,{"disambiguationData":[OSD([sQuery(id+"F0.wireOp",EDGE,"E18")])],"isStart":false});
            var Q9;
            Q9=makeQuery(id+"F9.opExtrude","SWEPT_EDGE",EDGE,{"disambiguationData":[OSD([sQuery(id+"F0.wireOp",EDGE,"E12"),sQuery(id+"F0.wireOp",EDGE,"E18")])]});
            var Q10;
            Q10=makeQuery(id+"F9.opExtrude","SWEPT_EDGE",EDGE,{"disambiguationData":[OSD([sQuery(id+"F0.wireOp",EDGE,"E12"),sQuery(id+"F0.wireOp",EDGE,"E19")])]});
            var Q11;
            Q11=makeQuery(id+"F9.opExtrude","SWEPT_EDGE",EDGE,{"disambiguationData":[OSD([sQuery(id+"F0.wireOp",EDGE,"E10"),sQuery(id+"F0.wireOp",EDGE,"E18")])]});
            var Q12;
            Q12=makeQuery(id+"F9.opExtrude","SWEPT_EDGE",EDGE,{"disambiguationData":[OSD([sQuery(id+"F0.wireOp",EDGE,"E10"),sQuery(id+"F0.wireOp",EDGE,"E19")])]});
            var Q13;
            Q13=makeQuery(id+"F8.opExtrude","CAP_EDGE",EDGE,{"disambiguationData":[OSD([sQuery(id+"F0.wireOp",EDGE,"E19")])],"isStart":false});
            var Q14;
            Q14=makeQuery(id+"F9.opExtrude","SWEPT_EDGE",EDGE,{"disambiguationData":[OSD([sQuery(id+"F0.wireOp",EDGE,"E14"),sQuery(id+"F0.wireOp",EDGE,"E16")])]});
            var Q15;
            Q15=makeQuery(id+"F9.opExtrude","CAP_EDGE",EDGE,{"disambiguationData":[OSD([sQuery(id+"F0.wireOp",EDGE,"E17.MirrorCS")])],"isStart":false});
            var Q16;
            {var subQ0=sQuery(id+"F0.wireOp",EDGE,"E12");Q16=makeQuery(id+"F9.opExtrude","CAP_EDGE",EDGE,{"disambiguationData":[OSD([subQ0]),TDD([makeQuery(id+"F0.imprint","IMPRINT",EDGE,{"disambiguationData":[TD([[makeQuery(id+"F0.imprint","INTERSECT",VERTEX,{"derivedFrom":[subQ0,sQuery(id+"F0.wireOp",EDGE,"E19")]}),-1.0]])],"derivedFrom":subQ0})])],"isStart":false});}
            fillet(context, id + "F16", {"entities" : qUnion([Q0, Q1, Q2, Q3, Q4, Q5, Q6, Q7, Q8, Q9, Q10, Q11, Q12, Q13, Q14, Q15, Q16]), "radius" : 1 * mm, "tangentPropagation" : true, "allowEdgeOverflow" : false});
        }
        {
            var Q0;
            Q0=makeQuery(id+"F7.opExtrude","SWEPT_FACE",FACE,{"disambiguationData":[OSD([sQuery(id+"F0.wireOp",EDGE,"E22")])]});
            var sketch = newSketch(context, id + "F17", { "sketchPlane" : qUnion([Q0])});
            skCircle(sketch, "E55", {"center": v(-72.75, 40) * mm, "radius": 2.75 * mm});
            skLineSegment(sketch, "E56", {"start": v(-72.75, 32.3) * mm, "end": v(-72.75, 46.4) * mm, "construction": true});
            skCircle(sketch, "E57", {"center": v(-72, 40) * mm, "radius": 2.75 * mm});
            skCircle(sketch, "E58.MirrorC", {"center": v(-73.5, 40) * mm, "radius": 2.75 * mm});
            skSolve(sketch);
        }
        {
            var Q0;
            {var subQ0=sQuery(id+"F17.wireOp",EDGE,"E58.MirrorC");var subQ1=sQuery(id+"F17.wireOp",EDGE,"E57");var subQ2=makeQuery(id+"F17.imprint","INTERSECT",VERTEX,{"disambiguationData":[OD(0.0)],"derivedFrom":[subQ1,subQ0]});Q0=makeQuery(id+"F17.imprint","IMPRINT",FACE,{"disambiguationData":[TD([[makeQuery(id+"F17.imprint","IMPRINT",EDGE,{"disambiguationData":[TD([[subQ2,-1.0]])],"derivedFrom":subQ1}),1.0]])]});}
            var Q1;
            {var subQ0=sQuery(id+"F17.wireOp",EDGE,"E57");var subQ1=sQuery(id+"F17.wireOp",EDGE,"E55");var subQ2=makeQuery(id+"F17.imprint","INTERSECT",VERTEX,{"disambiguationData":[OD(0.0)],"derivedFrom":[subQ1,subQ0]});Q1=makeQuery(id+"F17.imprint","IMPRINT",FACE,{"disambiguationData":[TD([[makeQuery(id+"F17.imprint","IMPRINT",EDGE,{"disambiguationData":[TD([[subQ2,1.0]])],"derivedFrom":subQ1}),1.0]])]});}
            var Q2;
            {var subQ0=sQuery(id+"F17.wireOp",EDGE,"E58.MirrorC");var subQ1=sQuery(id+"F17.wireOp",EDGE,"E55");var subQ2=makeQuery(id+"F17.imprint","INTERSECT",VERTEX,{"disambiguationData":[OD(0.0)],"derivedFrom":[subQ1,subQ0]});Q2=makeQuery(id+"F17.imprint","IMPRINT",FACE,{"disambiguationData":[TD([[makeQuery(id+"F17.imprint","IMPRINT",EDGE,{"disambiguationData":[TD([[subQ2,-1.0]])],"derivedFrom":subQ1}),-1.0]])]});}
            var Q3;
            {var subQ0=sQuery(id+"F17.wireOp",EDGE,"E58.MirrorC");var subQ1=sQuery(id+"F17.wireOp",EDGE,"E55");var subQ2=makeQuery(id+"F17.imprint","INTERSECT",VERTEX,{"disambiguationData":[OD(0.0)],"derivedFrom":[subQ1,subQ0]});Q3=makeQuery(id+"F17.imprint","IMPRINT",FACE,{"disambiguationData":[TD([[makeQuery(id+"F17.imprint","IMPRINT",EDGE,{"disambiguationData":[TD([[subQ2,-1.0]])],"derivedFrom":subQ1}),1.0]])]});}
            var Q4;
            {var subQ0=sQuery(id+"F17.wireOp",EDGE,"E57");var subQ1=sQuery(id+"F17.wireOp",EDGE,"E55");var subQ2=makeQuery(id+"F17.imprint","INTERSECT",VERTEX,{"disambiguationData":[OD(0.0)],"derivedFrom":[subQ1,subQ0]});Q4=makeQuery(id+"F17.imprint","IMPRINT",FACE,{"disambiguationData":[TD([[makeQuery(id+"F17.imprint","IMPRINT",EDGE,{"disambiguationData":[TD([[subQ2,1.0]])],"derivedFrom":subQ1}),-1.0]])]});}
            extrude(context, id + "F18", {"entities" : qUnion([Q0, Q1, Q2, Q3, Q4]), "operationType" : NewBodyOperationType.REMOVE, "oppositeDirection" : true, "depth" : 5 * mm});
        }
    });
